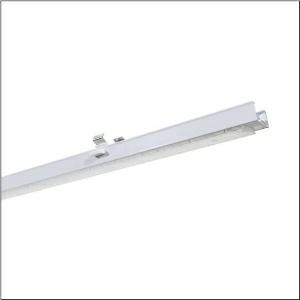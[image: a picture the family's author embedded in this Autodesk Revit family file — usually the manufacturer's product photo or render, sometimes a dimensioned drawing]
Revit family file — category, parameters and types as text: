
# Revit family: sanierungs-leuchteneinsatz_31_gen_2_51re12mb4cb_d6af
name_source: partatom
category: Lighting Fixtures
units: mm (PartAtom-declared; Revit-internal decimal feet)

## family parameters
Cut with Voids When Loaded = No
Host = Face
Light Source = No
Part Type = Normal
Room Calculation Point = No
Round Connector Dimension = Use Diameter
Shared = No

## types (1)
- --- (1 x LED, 11500 lm, 66 W, 4000K)
    Apparent Load = 66 VA
    CIE Flux Codes = 65 91 98 99 100
    Color Rendering = 80
    Color Temperature = 4000K
    Default Elevation = 1800 mm
    Description = Refurbishment luminaire insert Gen.2, luminaire insert, of extruded aluminium section, coated, traffic white (RAL 9016), length: 1.472mm, width: 91mm, height: 53mm, LED rated luminous flux: 11.500lm, light colour: 840, control gear: ON/OFF Multilumen, control gear: ECG Multilumen, with system connector: socket, mains connection: 220..240V, AC, 50/60Hz, connected load according to luminous flux setting (19/24/32/37/47/52/60/66W), luminous flux adjustable on luminaire in eight steps (3450/4380/5800/6700/8350/9200/10500/11500lm ), primary light control with lens, of plastic, primary optical cover: cover, of PMMA, light emission: direct distribution, protection rating (complete): IP20, insulation class (complete): insulation class I (protective earthing), certification: CE, UKCA, permissible ambient temperature for indoor applications: -20..+40°C, packaging unit: 1 piece
    Height = 58 mm
    Lamp = 1 x LED
    Lamp Light Flux = 11500 lm
    Lamp Power = 66 W
    Lamp count = 1
    Length = 1472 mm
    Luminous efficacy = 174 lm/W
    Manufacturer = Siteco
    ModVariant = No
    Model = 51RE12MB4CB
    Mounting Place = Ceiling
    Mounting Type = Pendant
    Number of Poles = 1
    OnlyDefault = Yes
    Power Factor = 1
    Product Name = Sanierungs-Leuchteneinsatz 31 Gen.2
    Product group = luminaire insert
    ProductGroupID = 902
    Protection Class = Protection class I
    Protection Degree = IP 20
    RLX_Detail_Level = 1
    RlxData = <blob elided: 21069 chars, md5=ab18e8a0>
    Socket = socket
    Standby Power = 0 W
    System Light Flux = 11500 lm
    System Power = 66 W
    Type Comments = factory setting: luminous flux: 100 % | (ON | ON | ON)
    Type Image = l_1266702.jpg
    URL = http://relux.com
    VarID = @adj_067977
    Voltage = 0 V
    Weight = 0.00 kg
    Width = 65 mm

## geometry (parser evidence)
native form markers: Blend x4, Sweep x13
no freeform markers — native parametric forms only
